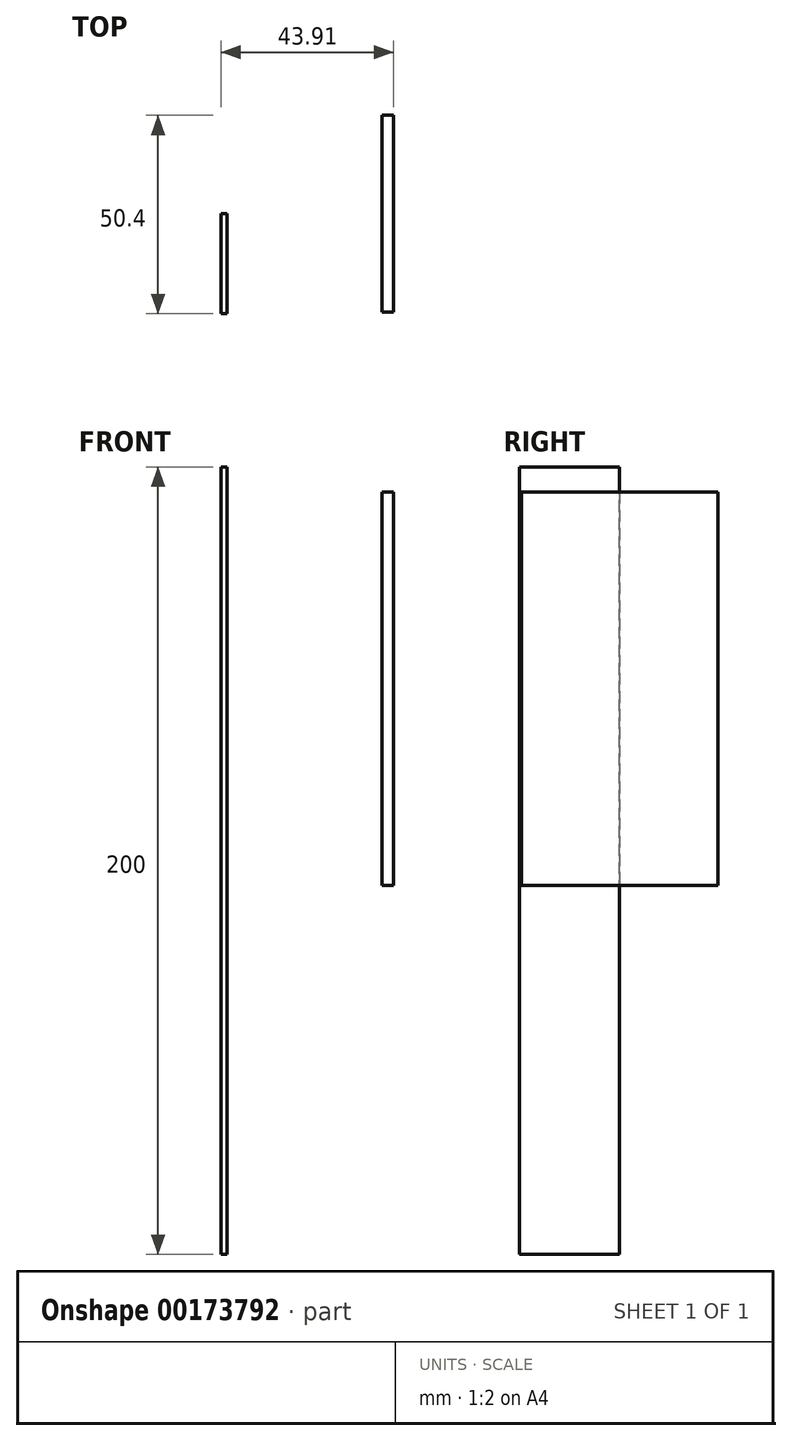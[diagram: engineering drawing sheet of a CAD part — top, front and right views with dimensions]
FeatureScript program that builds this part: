
annotation { "Feature Type Name" : "Feature", "Feature Type Description" : "" }
export const myFeature = defineFeature(function(context is Context, id is Id, definition is map)
    precondition{}
    {
        {
            var Q0;
            Q0=qCreatedBy(makeId("Front.planeOp"),FACE);
            var sketch = newSketch(context, id + "F0", { "sketchPlane" : qUnion([Q0])});
            skLineSegment(sketch, "E0", {"start": v(0, 66.97) * mm, "end": v(0, -33.03) * mm});
            skLineSegment(sketch, "E1", {"start": v(0, 66.97) * mm, "end": v(1.5, 66.97) * mm});
            skLineSegment(sketch, "E2", {"start": v(1.5, 66.97) * mm, "end": v(1.5, -33.03) * mm});
            skLineSegment(sketch, "E3", {"start": v(1.5, -33.03) * mm, "end": v(0, -33.03) * mm});
            skLineSegment(sketch, "E4", {"start": v(0, 66.97) * mm, "end": v(-1.5, 66.97) * mm});
            skLineSegment(sketch, "E5", {"start": v(-1.5, 66.97) * mm, "end": v(-1.5, -33.03) * mm});
            skLineSegment(sketch, "E6", {"start": v(-1.5, -33.03) * mm, "end": v(0, -33.03) * mm});
            skSolve(sketch);
        }
        {
            var Q0;
            Q0=makeQuery(id+"F0.imprint","IMPRINT",FACE,{"disambiguationData":[TD([[makeQuery(id+"F0.imprint","IMPRINT",EDGE,{"derivedFrom":sQuery(id+"F0.wireOp",EDGE,"E0")}),1.0]])]});
            var Q1;
            Q1=makeQuery(id+"F0.imprint","IMPRINT",FACE,{"disambiguationData":[TD([[makeQuery(id+"F0.imprint","IMPRINT",EDGE,{"derivedFrom":sQuery(id+"F0.wireOp",EDGE,"E0")}),-1.0]])]});
            extrude(context, id + "F1", {"entities" : qUnion([Q0, Q1]), "endBound" : BoundingType.SYMMETRIC, "depth" : 50 * mm});
        }
        {
            var Q0;
            Q0=qCreatedBy(makeId("Front.planeOp"),FACE);
            var sketch = newSketch(context, id + "F2", { "sketchPlane" : qUnion([Q0])});
            skLineSegment(sketch, "E7", {"start": v(-40.91, 73.25) * mm, "end": v(-40.91, -126.75) * mm});
            skLineSegment(sketch, "E8", {"start": v(-40.91, -126.75) * mm, "end": v(-42.41, -126.75) * mm});
            skLineSegment(sketch, "E9", {"start": v(-42.41, -126.75) * mm, "end": v(-42.41, 73.25) * mm});
            skLineSegment(sketch, "E10", {"start": v(-42.41, 73.25) * mm, "end": v(-40.91, 73.25) * mm});
            skSolve(sketch);
        }
        {
            var Q0;
            Q0 = qSketchRegion(id + "F2", true);
            extrude(context, id + "F3", {"entities" : qUnion([Q0]), "depth" : 25.4 * mm});
        }
    });
